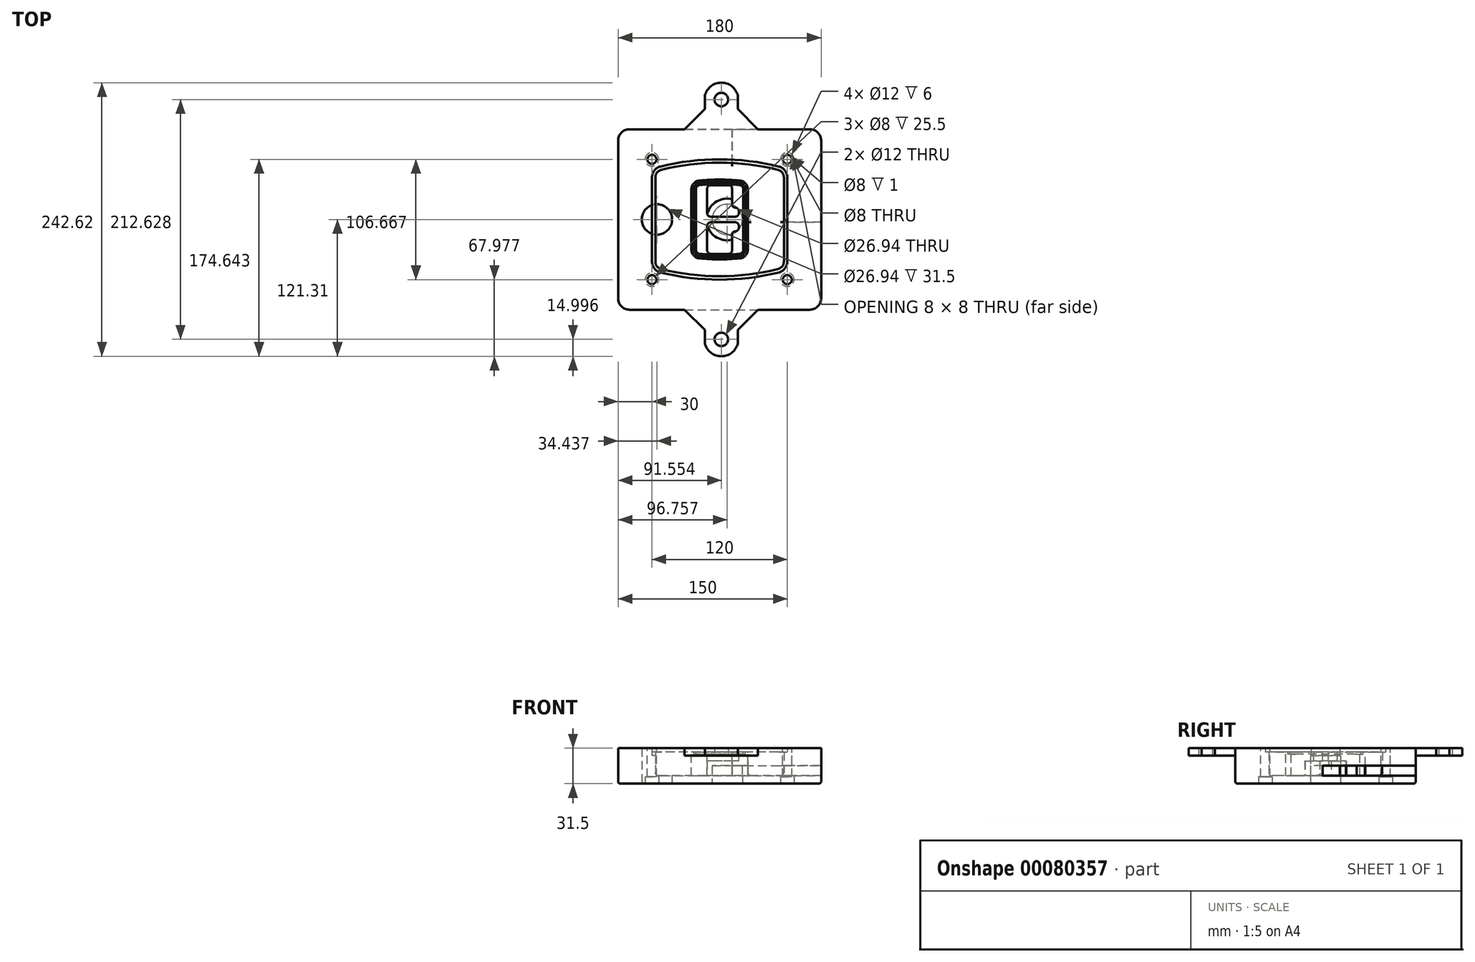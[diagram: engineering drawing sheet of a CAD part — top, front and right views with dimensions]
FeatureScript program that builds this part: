
annotation { "Feature Type Name" : "Feature", "Feature Type Description" : "" }
export const myFeature = defineFeature(function(context is Context, id is Id, definition is map)
    precondition{}
    {
        {
            var Q0;
            Q0=qCreatedBy(makeId("Top.planeOp"),FACE);
            var sketch = newSketch(context, id + "F0", { "sketchPlane" : qUnion([Q0])});
            skPoint(sketch, "E0.rect.middle", {"position": v(0, 0) * mm});
            skLineSegment(sketch, "E1.bottom", {"start": v(-80, -80) * mm, "end": v(80, -80) * mm});
            skLineSegment(sketch, "E1.top", {"start": v(-80, 80) * mm, "end": v(80, 80) * mm});
            skLineSegment(sketch, "E1.left", {"start": v(-90, -70) * mm, "end": v(-90, 70) * mm});
            skLineSegment(sketch, "E1.right", {"start": v(90, -70) * mm, "end": v(90, 70) * mm});
            skLineSegment(sketch, "E2", {"start": v(-90, 80) * mm, "end": v(90, -80) * mm, "construction": true});
            skLineSegment(sketch, "E3", {"start": v(90, 80) * mm, "end": v(-90, -80) * mm, "construction": true});
            skCircle(sketch, "E4", {"center": v(-60, 53.33) * mm, "radius": 4 * mm});
            skCircle(sketch, "E5", {"center": v(60, 53.33) * mm, "radius": 4 * mm});
            skCircle(sketch, "E6", {"center": v(60, -53.33) * mm, "radius": 4 * mm});
            skCircle(sketch, "E7", {"center": v(-60, -53.33) * mm, "radius": 4 * mm});
            skLineSegment(sketch, "E8", {"start": v(-60, 53.33) * mm, "end": v(60, 53.33) * mm, "construction": true});
            skLineSegment(sketch, "E9", {"start": v(60, 53.33) * mm, "end": v(60, -53.33) * mm, "construction": true});
            skLineSegment(sketch, "E10", {"start": v(60, -53.33) * mm, "end": v(-60, -53.33) * mm, "construction": true});
            skLineSegment(sketch, "E11", {"start": v(-60, -53.33) * mm, "end": v(-60, 53.33) * mm, "construction": true});
            skLineSegment(sketch, "E12", {"start": v(-60, 37.3) * mm, "end": v(-60, -37.3) * mm});
            skLineSegment(sketch, "E13", {"start": v(60, 37.3) * mm, "end": v(60, -37.3) * mm});
            skArc(sketch, "E14", {"start": v(52.38, 47.01) * mm, "mid": v(0, 53.33) * mm, "end": v(-52.38, 47.01) * mm});
            skArc(sketch, "E15", {"start": v(-52.38, -47.01) * mm, "mid": v(0, -53.33) * mm, "end": v(52.38, -47.01) * mm});
            skLineSegment(sketch, "E16", {"start": v(-60, 0) * mm, "end": v(60, 0) * mm, "construction": true});
            skPoint(sketch, "E17.visualSharp", {"position": v(-60, -45) * mm});
            skArc(sketch, "E17.filletArc", {"start": v(-60, -37.3) * mm, "mid": v(-57.87, -43.47) * mm, "end": v(-52.38, -47.01) * mm});
            skPoint(sketch, "E18.visualSharp", {"position": v(-60, 45) * mm});
            skArc(sketch, "E18.filletArc", {"start": v(-52.38, 47.01) * mm, "mid": v(-57.87, 43.47) * mm, "end": v(-60, 37.3) * mm});
            skPoint(sketch, "E19.visualSharp", {"position": v(60, 45) * mm});
            skArc(sketch, "E19.filletArc", {"start": v(60, 37.3) * mm, "mid": v(57.87, 43.47) * mm, "end": v(52.38, 47.01) * mm});
            skPoint(sketch, "E20.visualSharp", {"position": v(60, -45) * mm});
            skArc(sketch, "E20.filletArc", {"start": v(52.38, -47.01) * mm, "mid": v(57.87, -43.47) * mm, "end": v(60, -37.3) * mm});
            skPoint(sketch, "E21.visualSharp", {"position": v(-90, 80) * mm});
            skArc(sketch, "E21.filletArc", {"start": v(-80, 80) * mm, "mid": v(-87.07, 77.07) * mm, "end": v(-90, 70) * mm});
            skPoint(sketch, "E22.visualSharp", {"position": v(90, 80) * mm});
            skArc(sketch, "E22.filletArc", {"start": v(90, 70) * mm, "mid": v(87.07, 77.07) * mm, "end": v(80, 80) * mm});
            skPoint(sketch, "E23.visualSharp", {"position": v(90, -80) * mm});
            skArc(sketch, "E23.filletArc", {"start": v(80, -80) * mm, "mid": v(87.07, -77.07) * mm, "end": v(90, -70) * mm});
            skPoint(sketch, "E24.visualSharp", {"position": v(-90, -80) * mm});
            skArc(sketch, "E24.filletArc", {"start": v(-90, -70) * mm, "mid": v(-87.07, -77.07) * mm, "end": v(-80, -80) * mm});
            skArc(sketch, "E25.0", {"start": v(57, 37.3) * mm, "mid": v(55.5, 41.62) * mm, "end": v(51.67, 44.1) * mm});
            skLineSegment(sketch, "E25.1", {"start": v(57, 37.3) * mm, "end": v(57, -37.3) * mm});
            skArc(sketch, "E25.2", {"start": v(51.67, -44.1) * mm, "mid": v(55.5, -41.62) * mm, "end": v(57, -37.3) * mm});
            skArc(sketch, "E25.3", {"start": v(-51.67, -44.1) * mm, "mid": v(0, -50.33) * mm, "end": v(51.67, -44.1) * mm});
            skArc(sketch, "E25.4", {"start": v(-57, -37.3) * mm, "mid": v(-55.5, -41.62) * mm, "end": v(-51.67, -44.1) * mm});
            skArc(sketch, "E25.5", {"start": v(51.67, 44.1) * mm, "mid": v(0, 50.33) * mm, "end": v(-51.67, 44.1) * mm});
            skLineSegment(sketch, "E25.6", {"start": v(-57, 37.3) * mm, "end": v(-57, -37.3) * mm});
            skArc(sketch, "E25.7", {"start": v(-51.67, 44.1) * mm, "mid": v(-55.5, 41.62) * mm, "end": v(-57, 37.3) * mm});
            skArc(sketch, "E26.0", {"start": v(-53.33, 50.9) * mm, "mid": v(-61.01, 45.94) * mm, "end": v(-64, 37.3) * mm});
            skArc(sketch, "E26.1", {"start": v(53.33, 50.9) * mm, "mid": v(0, 57.33) * mm, "end": v(-53.33, 50.9) * mm});
            skArc(sketch, "E26.2", {"start": v(64, 37.3) * mm, "mid": v(61.01, 45.94) * mm, "end": v(53.33, 50.9) * mm});
            skLineSegment(sketch, "E26.3", {"start": v(64, 37.3) * mm, "end": v(64, -37.3) * mm});
            skArc(sketch, "E26.4", {"start": v(53.33, -50.9) * mm, "mid": v(61.01, -45.94) * mm, "end": v(64, -37.3) * mm});
            skLineSegment(sketch, "E26.5", {"start": v(-64, 37.3) * mm, "end": v(-64, -37.3) * mm});
            skArc(sketch, "E26.6", {"start": v(-53.33, -50.9) * mm, "mid": v(0, -57.33) * mm, "end": v(53.33, -50.9) * mm});
            skArc(sketch, "E26.7", {"start": v(-64, -37.3) * mm, "mid": v(-61.01, -45.94) * mm, "end": v(-53.33, -50.9) * mm});
            skSolve(sketch);
        }
        {
            var Q0;
            Q0=makeQuery(id+"F0.imprint","IMPRINT",FACE,{"disambiguationData":[TD([[makeQuery(id+"F0.imprint","IMPRINT",EDGE,{"derivedFrom":sQuery(id+"F0.wireOp",EDGE,"E1.bottom")}),1.0]])]});
            var Q1;
            Q1=makeQuery(id+"F0.imprint","IMPRINT",FACE,{"disambiguationData":[TD([[makeQuery(id+"F0.imprint","IMPRINT",EDGE,{"derivedFrom":sQuery(id+"F0.wireOp",EDGE,"E12")}),1.0]])]});
            var Q2;
            Q2=makeQuery(id+"F0.imprint","IMPRINT",FACE,{"disambiguationData":[TD([[makeQuery(id+"F0.imprint","IMPRINT",EDGE,{"derivedFrom":sQuery(id+"F0.wireOp",EDGE,"E25.0")}),1.0]])]});
            var Q3;
            Q3=makeQuery(id+"F0.imprint","IMPRINT",FACE,{"disambiguationData":[TD([[makeQuery(id+"F0.imprint","IMPRINT",EDGE,{"derivedFrom":sQuery(id+"F0.wireOp",EDGE,"E12")}),-1.0]])]});
            extrude(context, id + "F1", {"entities" : qUnion([Q0, Q1, Q2, Q3]), "oppositeDirection" : true, "depth" : 25 * mm});
        }
        {
            var Q0;
            Q0=makeQuery(id+"F0.imprint","IMPRINT",FACE,{"disambiguationData":[TD([[makeQuery(id+"F0.imprint","IMPRINT",EDGE,{"derivedFrom":sQuery(id+"F0.wireOp",EDGE,"E12")}),1.0]])]});
            extrude(context, id + "F2", {"entities" : qUnion([Q0]), "operationType" : NewBodyOperationType.ADD, "depth" : 3 * mm});
        }
        {
            var Q0;
            Q0=makeQuery(id+"F0.imprint","IMPRINT",FACE,{"disambiguationData":[TD([[makeQuery(id+"F0.imprint","IMPRINT",EDGE,{"derivedFrom":sQuery(id+"F0.wireOp",EDGE,"E25.0")}),1.0]])]});
            extrude(context, id + "F3", {"entities" : qUnion([Q0]), "operationType" : NewBodyOperationType.REMOVE, "oppositeDirection" : true, "depth" : 18 * mm});
        }
        {
            var Q0;
            Q0=makeQuery(id+"F2.opExtrude","CAP_FACE",FACE,{"disambiguationData":[OSD([sQuery(id+"F0.wireOp",EDGE,"E12"),sQuery(id+"F0.wireOp",EDGE,"E13"),sQuery(id+"F0.wireOp",EDGE,"E14"),sQuery(id+"F0.wireOp",EDGE,"E15"),sQuery(id+"F0.wireOp",EDGE,"E17.filletArc"),sQuery(id+"F0.wireOp",EDGE,"E18.filletArc"),sQuery(id+"F0.wireOp",EDGE,"E19.filletArc"),sQuery(id+"F0.wireOp",EDGE,"E20.filletArc"),sQuery(id+"F0.wireOp",EDGE,"E25.0"),sQuery(id+"F0.wireOp",EDGE,"E25.1"),sQuery(id+"F0.wireOp",EDGE,"E25.2"),sQuery(id+"F0.wireOp",EDGE,"E25.3"),sQuery(id+"F0.wireOp",EDGE,"E25.4"),sQuery(id+"F0.wireOp",EDGE,"E25.5"),sQuery(id+"F0.wireOp",EDGE,"E25.6"),sQuery(id+"F0.wireOp",EDGE,"E25.7")])],"isStart":false});
            var sketch = newSketch(context, id + "F4", { "sketchPlane" : qUnion([Q0])});
            skArc(sketch, "E27.0", {"start": v(-17.7, -34.56) * mm, "mid": v(0, -35.33) * mm, "end": v(17.7, -34.56) * mm});
            skArc(sketch, "E28.0", {"start": v(17.7, 34.56) * mm, "mid": v(0, 35.33) * mm, "end": v(-17.7, 34.56) * mm});
            skLineSegment(sketch, "E29", {"start": v(-25, 26.59) * mm, "end": v(-25, -26.59) * mm});
            skLineSegment(sketch, "E30", {"start": v(25, 26.59) * mm, "end": v(25, -26.59) * mm});
            skLineSegment(sketch, "E31", {"start": v(-25, 33.78) * mm, "end": v(25, 33.78) * mm, "construction": true});
            skLineSegment(sketch, "E32", {"start": v(-25, -33.78) * mm, "end": v(25, -33.78) * mm, "construction": true});
            skPoint(sketch, "E33.visualSharp", {"position": v(-25, 33.78) * mm});
            skArc(sketch, "E33.filletArc", {"start": v(-17.7, 34.56) * mm, "mid": v(-22.9, 32) * mm, "end": v(-25, 26.59) * mm});
            skPoint(sketch, "E34.visualSharp", {"position": v(25, 33.78) * mm});
            skArc(sketch, "E34.filletArc", {"start": v(25, 26.59) * mm, "mid": v(22.9, 32) * mm, "end": v(17.7, 34.56) * mm});
            skPoint(sketch, "E35.visualSharp", {"position": v(25, -33.78) * mm});
            skArc(sketch, "E35.filletArc", {"start": v(17.7, -34.56) * mm, "mid": v(22.9, -32) * mm, "end": v(25, -26.59) * mm});
            skPoint(sketch, "E36.visualSharp", {"position": v(-25, -33.78) * mm});
            skArc(sketch, "E36.filletArc", {"start": v(-25, -26.59) * mm, "mid": v(-22.9, -32) * mm, "end": v(-17.7, -34.56) * mm});
            skArc(sketch, "E37.0", {"start": v(51.67, 44.1) * mm, "mid": v(0, 50.33) * mm, "end": v(-51.67, 44.1) * mm});
            skArc(sketch, "E37.1", {"start": v(-51.67, 44.1) * mm, "mid": v(-55.5, 41.62) * mm, "end": v(-57, 37.3) * mm});
            skLineSegment(sketch, "E37.2", {"start": v(-57, 37.3) * mm, "end": v(-57, -37.3) * mm});
            skArc(sketch, "E37.3", {"start": v(-57, -37.3) * mm, "mid": v(-55.5, -41.62) * mm, "end": v(-51.67, -44.1) * mm});
            skArc(sketch, "E37.4", {"start": v(-51.67, -44.1) * mm, "mid": v(0, -50.33) * mm, "end": v(51.67, -44.1) * mm});
            skArc(sketch, "E37.5", {"start": v(51.67, -44.1) * mm, "mid": v(55.5, -41.62) * mm, "end": v(57, -37.3) * mm});
            skLineSegment(sketch, "E37.6", {"start": v(57, 37.3) * mm, "end": v(57, -37.3) * mm});
            skArc(sketch, "E37.7", {"start": v(57, 37.3) * mm, "mid": v(55.5, 41.62) * mm, "end": v(51.67, 44.1) * mm});
            skLineSegment(sketch, "E38.0", {"start": v(23, 26.59) * mm, "end": v(23, -26.59) * mm});
            skArc(sketch, "E38.1", {"start": v(17.53, -32.56) * mm, "mid": v(21.42, -30.64) * mm, "end": v(23, -26.59) * mm});
            skArc(sketch, "E38.2", {"start": v(-17.53, -32.56) * mm, "mid": v(0, -33.33) * mm, "end": v(17.53, -32.56) * mm});
            skArc(sketch, "E38.3", {"start": v(-23, -26.59) * mm, "mid": v(-21.42, -30.64) * mm, "end": v(-17.53, -32.56) * mm});
            skLineSegment(sketch, "E38.4", {"start": v(-23, 26.59) * mm, "end": v(-23, -26.59) * mm});
            skArc(sketch, "E38.5", {"start": v(23, 26.59) * mm, "mid": v(21.42, 30.64) * mm, "end": v(17.53, 32.56) * mm});
            skArc(sketch, "E38.6", {"start": v(-17.53, 32.56) * mm, "mid": v(-21.42, 30.64) * mm, "end": v(-23, 26.59) * mm});
            skArc(sketch, "E38.7", {"start": v(17.53, 32.56) * mm, "mid": v(0, 33.33) * mm, "end": v(-17.53, 32.56) * mm});
            skArc(sketch, "E39.0", {"start": v(21, 26.59) * mm, "mid": v(19.95, 29.29) * mm, "end": v(17.35, 30.57) * mm});
            skLineSegment(sketch, "E39.1", {"start": v(21, 26.59) * mm, "end": v(21, -26.59) * mm});
            skArc(sketch, "E39.2", {"start": v(17.35, -30.57) * mm, "mid": v(19.95, -29.29) * mm, "end": v(21, -26.59) * mm});
            skArc(sketch, "E39.3", {"start": v(-17.35, -30.57) * mm, "mid": v(0, -31.33) * mm, "end": v(17.35, -30.57) * mm});
            skArc(sketch, "E39.4", {"start": v(-21, -26.59) * mm, "mid": v(-19.95, -29.29) * mm, "end": v(-17.35, -30.57) * mm});
            skArc(sketch, "E39.5", {"start": v(17.35, 30.57) * mm, "mid": v(0, 31.33) * mm, "end": v(-17.35, 30.57) * mm});
            skLineSegment(sketch, "E39.6", {"start": v(-21, 26.59) * mm, "end": v(-21, -26.59) * mm});
            skArc(sketch, "E39.7", {"start": v(-17.35, 30.57) * mm, "mid": v(-19.95, 29.29) * mm, "end": v(-21, 26.59) * mm});
            skLineSegment(sketch, "E40", {"start": v(-25, 0) * mm, "end": v(25, 0) * mm, "construction": true});
            skLineSegment(sketch, "E41", {"start": v(-11, 5.5) * mm, "end": v(-11, 27.5) * mm});
            skLineSegment(sketch, "E42", {"start": v(-8, 30.5) * mm, "end": v(8, 30.5) * mm});
            skLineSegment(sketch, "E43", {"start": v(11, 27.5) * mm, "end": v(11, 13.5) * mm});
            skLineSegment(sketch, "E44", {"start": v(14, 10.5) * mm, "end": v(14, 10.5) * mm});
            skLineSegment(sketch, "E45", {"start": v(17, 7.5) * mm, "end": v(17, 5.5) * mm});
            skLineSegment(sketch, "E46", {"start": v(14, 2.5) * mm, "end": v(-8, 2.5) * mm});
            skPoint(sketch, "E47.visualSharp", {"position": v(-11, 30.5) * mm});
            skArc(sketch, "E47.filletArc", {"start": v(-8, 30.5) * mm, "mid": v(-10.12, 29.62) * mm, "end": v(-11, 27.5) * mm});
            skPoint(sketch, "E48.visualSharp", {"position": v(11, 30.5) * mm});
            skArc(sketch, "E48.filletArc", {"start": v(11, 27.5) * mm, "mid": v(10.12, 29.62) * mm, "end": v(8, 30.5) * mm});
            skPoint(sketch, "E49.visualSharp", {"position": v(11, 10.5) * mm});
            skArc(sketch, "E49.filletArc", {"start": v(11, 13.5) * mm, "mid": v(11.88, 11.38) * mm, "end": v(14, 10.5) * mm});
            skPoint(sketch, "E50.visualSharp", {"position": v(17, 10.5) * mm});
            skArc(sketch, "E50.filletArc", {"start": v(17, 7.5) * mm, "mid": v(16.12, 9.62) * mm, "end": v(14, 10.5) * mm});
            skPoint(sketch, "E51.visualSharp", {"position": v(17, 2.5) * mm});
            skArc(sketch, "E51.filletArc", {"start": v(14, 2.5) * mm, "mid": v(16.12, 3.38) * mm, "end": v(17, 5.5) * mm});
            skPoint(sketch, "E52.visualSharp", {"position": v(-11, 2.5) * mm});
            skArc(sketch, "E52.filletArc", {"start": v(-11, 5.5) * mm, "mid": v(-10.12, 3.38) * mm, "end": v(-8, 2.5) * mm});
            skLineSegment(sketch, "E53.0.MirrorCS", {"start": v(14, -2.5) * mm, "end": v(-8, -2.5) * mm});
            skArc(sketch, "E54.0.MirrorCS", {"start": v(-11, -5.5) * mm, "mid": v(-10.12, -3.38) * mm, "end": v(-8, -2.5) * mm});
            skLineSegment(sketch, "E55.0.MirrorCS", {"start": v(-11, -5.5) * mm, "end": v(-11, -27.5) * mm});
            skArc(sketch, "E56.0.MirrorCS", {"start": v(-8, -30.5) * mm, "mid": v(-10.12, -29.62) * mm, "end": v(-11, -27.5) * mm});
            skLineSegment(sketch, "E57.0.MirrorCS", {"start": v(-8, -30.5) * mm, "end": v(8, -30.5) * mm});
            skArc(sketch, "E58.0.MirrorCS", {"start": v(11, -27.5) * mm, "mid": v(10.12, -29.62) * mm, "end": v(8, -30.5) * mm});
            skLineSegment(sketch, "E59.0.MirrorCS", {"start": v(11, -27.5) * mm, "end": v(11, -13.5) * mm});
            skArc(sketch, "E60.0.MirrorCS", {"start": v(11, -13.5) * mm, "mid": v(11.88, -11.38) * mm, "end": v(14, -10.5) * mm});
            skArc(sketch, "E61.0.MirrorCS", {"start": v(17, -7.5) * mm, "mid": v(16.12, -9.62) * mm, "end": v(14, -10.5) * mm});
            skLineSegment(sketch, "E62.0.MirrorCS", {"start": v(17, -7.5) * mm, "end": v(17, -5.5) * mm});
            skArc(sketch, "E63.0.MirrorCS", {"start": v(14, -2.5) * mm, "mid": v(16.12, -3.38) * mm, "end": v(17, -5.5) * mm});
            skSolve(sketch);
        }
        {
            var Q0;
            Q0=makeQuery(id+"F4.imprint","IMPRINT",FACE,{"disambiguationData":[TD([[makeQuery(id+"F4.imprint","IMPRINT",EDGE,{"derivedFrom":sQuery(id+"F4.wireOp",EDGE,"E27.0")}),1.0]])]});
            var Q1;
            Q1=makeQuery(id+"F4.imprint","IMPRINT",FACE,{"disambiguationData":[TD([[makeQuery(id+"F4.imprint","IMPRINT",EDGE,{"derivedFrom":sQuery(id+"F4.wireOp",EDGE,"E38.0")}),-1.0]])]});
            var Q2;
            Q2=makeQuery(id+"F4.imprint","IMPRINT",FACE,{"disambiguationData":[TD([[makeQuery(id+"F4.imprint","IMPRINT",EDGE,{"derivedFrom":sQuery(id+"F4.wireOp",EDGE,"E39.0")}),1.0]])]});
            extrude(context, id + "F5", {"entities" : qUnion([Q0, Q1, Q2]), "operationType" : NewBodyOperationType.ADD, "endBound" : BoundingType.UP_TO_NEXT, "oppositeDirection" : true, "depth" : 25 * mm});
        }
        {
            var Q0;
            Q0=makeQuery(id+"F4.imprint","IMPRINT",FACE,{"disambiguationData":[TD([[makeQuery(id+"F4.imprint","IMPRINT",EDGE,{"derivedFrom":sQuery(id+"F4.wireOp",EDGE,"E38.0")}),-1.0]])]});
            extrude(context, id + "F6", {"entities" : qUnion([Q0]), "operationType" : NewBodyOperationType.REMOVE, "oppositeDirection" : true, "depth" : 2 * mm});
        }
        {
            var Q0;
            Q0=makeQuery(id+"F1.opExtrude","CAP_FACE",FACE,{"disambiguationData":[OSD([sQuery(id+"F0.wireOp",EDGE,"E1.bottom"),sQuery(id+"F0.wireOp",EDGE,"E1.top"),sQuery(id+"F0.wireOp",EDGE,"E1.left"),sQuery(id+"F0.wireOp",EDGE,"E1.right"),sQuery(id+"F0.wireOp",EDGE,"E4"),sQuery(id+"F0.wireOp",EDGE,"E5"),sQuery(id+"F0.wireOp",EDGE,"E6"),sQuery(id+"F0.wireOp",EDGE,"E7"),sQuery(id+"F0.wireOp",EDGE,"E21.filletArc"),sQuery(id+"F0.wireOp",EDGE,"E22.filletArc"),sQuery(id+"F0.wireOp",EDGE,"E23.filletArc"),sQuery(id+"F0.wireOp",EDGE,"E24.filletArc")])],"isStart":false});
            var sketch = newSketch(context, id + "F7", { "sketchPlane" : qUnion([Q0])});
            skCircle(sketch, "E64", {"center": v(6.76, 0) * mm, "radius": 13.47 * mm});
            skCircle(sketch, "E65", {"center": v(-55.56, 0) * mm, "radius": 13.47 * mm});
            skLineSegment(sketch, "E66", {"start": v(90, 0) * mm, "end": v(-90, 0) * mm});
            skCircle(sketch, "E67", {"center": v(6.76, 0) * mm, "radius": 18.47 * mm});
            skCircle(sketch, "E68", {"center": v(60, -53.33) * mm, "radius": 6 * mm});
            skCircle(sketch, "E69", {"center": v(-60, -53.33) * mm, "radius": 6 * mm});
            skCircle(sketch, "E70", {"center": v(-60, 53.33) * mm, "radius": 6 * mm});
            skCircle(sketch, "E71", {"center": v(60, 53.33) * mm, "radius": 6 * mm});
            skSolve(sketch);
        }
        {
            var Q0;
            {var subQ1=sQuery(id+"F7.wireOp",EDGE,"E66");var subQ4=sQuery(id+"F7.wireOp",EDGE,"E64");var subQ6=makeQuery(id+"F7.imprint","INTERSECT",VERTEX,{"disambiguationData":[OD(0.0)],"derivedFrom":[subQ4,subQ1]});Q0=makeQuery(id+"F7.imprint","IMPRINT",FACE,{"disambiguationData":[TD([[makeQuery(id+"F7.imprint","IMPRINT",EDGE,{"disambiguationData":[TD([[subQ6,-1.0]])],"derivedFrom":subQ4}),-1.0]])]});}
            var Q1;
            {var subQ0=sQuery(id+"F7.wireOp",EDGE,"E66");var subQ1=sQuery(id+"F7.wireOp",EDGE,"E64");var subQ3=makeQuery(id+"F7.imprint","INTERSECT",VERTEX,{"disambiguationData":[OD(0.0)],"derivedFrom":[subQ1,subQ0]});Q1=makeQuery(id+"F7.imprint","IMPRINT",FACE,{"disambiguationData":[TD([[makeQuery(id+"F7.imprint","IMPRINT",EDGE,{"disambiguationData":[TD([[subQ3,-1.0]])],"derivedFrom":subQ1}),1.0]])]});}
            var Q2;
            {var subQ0=sQuery(id+"F7.wireOp",EDGE,"E66");var subQ1=sQuery(id+"F7.wireOp",EDGE,"E64");var subQ3=makeQuery(id+"F7.imprint","INTERSECT",VERTEX,{"disambiguationData":[OD(0.0)],"derivedFrom":[subQ1,subQ0]});Q2=makeQuery(id+"F7.imprint","IMPRINT",FACE,{"disambiguationData":[TD([[makeQuery(id+"F7.imprint","IMPRINT",EDGE,{"disambiguationData":[TD([[subQ3,1.0]])],"derivedFrom":subQ1}),1.0]])]});}
            var Q3;
            {var subQ1=sQuery(id+"F7.wireOp",EDGE,"E66");var subQ4=sQuery(id+"F7.wireOp",EDGE,"E64");var subQ6=makeQuery(id+"F7.imprint","INTERSECT",VERTEX,{"disambiguationData":[OD(0.0)],"derivedFrom":[subQ4,subQ1]});Q3=makeQuery(id+"F7.imprint","IMPRINT",FACE,{"disambiguationData":[TD([[makeQuery(id+"F7.imprint","IMPRINT",EDGE,{"disambiguationData":[TD([[subQ6,1.0]])],"derivedFrom":subQ4}),-1.0]])]});}
            extrude(context, id + "F8", {"entities" : qUnion([Q0, Q1, Q2, Q3]), "operationType" : NewBodyOperationType.ADD, "oppositeDirection" : true, "depth" : 20 * mm});
        }
        {
            var Q0;
            {var subQ0=sQuery(id+"F7.wireOp",EDGE,"E66");var subQ1=sQuery(id+"F7.wireOp",EDGE,"E64");var subQ3=makeQuery(id+"F7.imprint","INTERSECT",VERTEX,{"disambiguationData":[OD(0.0)],"derivedFrom":[subQ1,subQ0]});Q0=makeQuery(id+"F7.imprint","IMPRINT",FACE,{"disambiguationData":[TD([[makeQuery(id+"F7.imprint","IMPRINT",EDGE,{"disambiguationData":[TD([[subQ3,-1.0]])],"derivedFrom":subQ1}),1.0]])]});}
            var Q1;
            {var subQ0=sQuery(id+"F7.wireOp",EDGE,"E66");var subQ1=sQuery(id+"F7.wireOp",EDGE,"E64");var subQ3=makeQuery(id+"F7.imprint","INTERSECT",VERTEX,{"disambiguationData":[OD(0.0)],"derivedFrom":[subQ1,subQ0]});Q1=makeQuery(id+"F7.imprint","IMPRINT",FACE,{"disambiguationData":[TD([[makeQuery(id+"F7.imprint","IMPRINT",EDGE,{"disambiguationData":[TD([[subQ3,1.0]])],"derivedFrom":subQ1}),1.0]])]});}
            extrude(context, id + "F9", {"entities" : qUnion([Q0, Q1]), "operationType" : NewBodyOperationType.REMOVE, "oppositeDirection" : true, "depth" : 16 * mm});
        }
        {
            var Q0;
            {var subQ0=sQuery(id+"F7.wireOp",EDGE,"E66");var subQ1=sQuery(id+"F7.wireOp",EDGE,"E65");var subQ3=makeQuery(id+"F7.imprint","INTERSECT",VERTEX,{"disambiguationData":[OD(0.0)],"derivedFrom":[subQ1,subQ0]});Q0=makeQuery(id+"F7.imprint","IMPRINT",FACE,{"disambiguationData":[TD([[makeQuery(id+"F7.imprint","IMPRINT",EDGE,{"disambiguationData":[TD([[subQ3,-1.0]])],"derivedFrom":subQ1}),1.0]])]});}
            var Q1;
            {var subQ0=sQuery(id+"F7.wireOp",EDGE,"E66");var subQ1=sQuery(id+"F7.wireOp",EDGE,"E65");var subQ3=makeQuery(id+"F7.imprint","INTERSECT",VERTEX,{"disambiguationData":[OD(0.0)],"derivedFrom":[subQ1,subQ0]});Q1=makeQuery(id+"F7.imprint","IMPRINT",FACE,{"disambiguationData":[TD([[makeQuery(id+"F7.imprint","IMPRINT",EDGE,{"disambiguationData":[TD([[subQ3,1.0]])],"derivedFrom":subQ1}),1.0]])]});}
            extrude(context, id + "F10", {"entities" : qUnion([Q0, Q1]), "operationType" : NewBodyOperationType.REMOVE, "oppositeDirection" : true, "depth" : 25 * mm});
        }
        {
            var Q0;
            Q0=makeQuery(id+"F7.imprint","IMPRINT",FACE,{"disambiguationData":[TD([[makeQuery(id+"F7.imprint","IMPRINT",EDGE,{"derivedFrom":sQuery(id+"F7.wireOp",EDGE,"E68")}),1.0]])]});
            var Q1;
            Q1=makeQuery(id+"F7.imprint","IMPRINT",FACE,{"disambiguationData":[TD([[makeQuery(id+"F7.imprint","IMPRINT",EDGE,{"derivedFrom":makeQuery(id+"F1.opExtrude","CAP_EDGE",EDGE,{"disambiguationData":[OSD([sQuery(id+"F0.wireOp",EDGE,"E5")])],"isStart":false})}),-1.0]])]});
            var Q2;
            Q2=makeQuery(id+"F7.imprint","IMPRINT",FACE,{"disambiguationData":[TD([[makeQuery(id+"F7.imprint","IMPRINT",EDGE,{"derivedFrom":sQuery(id+"F7.wireOp",EDGE,"E69")}),1.0]])]});
            var Q3;
            Q3=makeQuery(id+"F7.imprint","IMPRINT",FACE,{"disambiguationData":[TD([[makeQuery(id+"F7.imprint","IMPRINT",EDGE,{"derivedFrom":makeQuery(id+"F1.opExtrude","CAP_EDGE",EDGE,{"disambiguationData":[OSD([sQuery(id+"F0.wireOp",EDGE,"E4")])],"isStart":false})}),-1.0]])]});
            var Q4;
            Q4=makeQuery(id+"F7.imprint","IMPRINT",FACE,{"disambiguationData":[TD([[makeQuery(id+"F7.imprint","IMPRINT",EDGE,{"derivedFrom":sQuery(id+"F7.wireOp",EDGE,"E70")}),1.0]])]});
            var Q5;
            Q5=makeQuery(id+"F7.imprint","IMPRINT",FACE,{"disambiguationData":[TD([[makeQuery(id+"F7.imprint","IMPRINT",EDGE,{"derivedFrom":makeQuery(id+"F1.opExtrude","CAP_EDGE",EDGE,{"disambiguationData":[OSD([sQuery(id+"F0.wireOp",EDGE,"E7")])],"isStart":false})}),-1.0]])]});
            var Q6;
            Q6=makeQuery(id+"F7.imprint","IMPRINT",FACE,{"disambiguationData":[TD([[makeQuery(id+"F7.imprint","IMPRINT",EDGE,{"derivedFrom":sQuery(id+"F7.wireOp",EDGE,"E71")}),1.0]])]});
            var Q7;
            Q7=makeQuery(id+"F7.imprint","IMPRINT",FACE,{"disambiguationData":[TD([[makeQuery(id+"F7.imprint","IMPRINT",EDGE,{"derivedFrom":makeQuery(id+"F1.opExtrude","CAP_EDGE",EDGE,{"disambiguationData":[OSD([sQuery(id+"F0.wireOp",EDGE,"E6")])],"isStart":false})}),-1.0]])]});
            extrude(context, id + "F11", {"entities" : qUnion([Q0, Q1, Q2, Q3, Q4, Q5, Q6, Q7]), "operationType" : NewBodyOperationType.REMOVE, "oppositeDirection" : true, "depth" : 6 * mm});
        }
        {
            var Q0;
            Q0=makeQuery(id+"F9.boolean.opBoolean","COPY",FACE,{"derivedFrom":makeQuery(id+"F9.opExtrude","CAP_FACE",FACE,{"disambiguationData":[OSD([sQuery(id+"F7.wireOp",EDGE,"E64")])],"isStart":false})});
            var sketch = newSketch(context, id + "F12", { "sketchPlane" : qUnion([Q0])});
            skArc(sketch, "E72.0", {"start": v(11, -88.19) * mm, "mid": v(97.1, -83.6) * mm, "end": v(92.5, 2.5) * mm});
            skLineSegment(sketch, "E72.1", {"start": v(11, -17.97) * mm, "end": v(11, -17.97) * mm});
            skLineSegment(sketch, "E73", {"start": v(92.5, -105.13) * mm, "end": v(102.3, -105.13) * mm});
            skLineSegment(sketch, "E74.0", {"start": v(92.5, 2.5) * mm, "end": v(14, 2.5) * mm});
            skArc(sketch, "E74.1", {"start": v(14, 2.5) * mm, "mid": v(16.12, 3.38) * mm, "end": v(17, 5.5) * mm});
            skLineSegment(sketch, "E74.2", {"start": v(17, 7.5) * mm, "end": v(17, 5.5) * mm});
            skArc(sketch, "E74.3", {"start": v(17, 7.5) * mm, "mid": v(16.12, 9.62) * mm, "end": v(14, 10.5) * mm});
            skArc(sketch, "E74.4", {"start": v(11, 13.5) * mm, "mid": v(11.88, 11.38) * mm, "end": v(14, 10.5) * mm});
            skLineSegment(sketch, "E74.5", {"start": v(11, 13.5) * mm, "end": v(11, -88.19) * mm});
            skLineSegment(sketch, "E74.7", {"start": v(92.5, -2.5) * mm, "end": v(14, -2.5) * mm});
            skArc(sketch, "E74.8", {"start": v(14, -2.5) * mm, "mid": v(16.12, -3.38) * mm, "end": v(17, -5.5) * mm});
            skLineSegment(sketch, "E74.9", {"start": v(17, -7.5) * mm, "end": v(17, -5.5) * mm});
            skArc(sketch, "E74.10", {"start": v(17, -7.5) * mm, "mid": v(16.12, -9.62) * mm, "end": v(14, -10.5) * mm});
            skArc(sketch, "E74.11", {"start": v(11, -13.5) * mm, "mid": v(11.88, -11.38) * mm, "end": v(14, -10.5) * mm});
            skLineSegment(sketch, "E74.12", {"start": v(11, -17.97) * mm, "end": v(11, -13.5) * mm});
            skPoint(sketch, "E75.orphan", {"position": v(11, -27.5) * mm});
            skPoint(sketch, "E76.orphan", {"position": v(-8, -2.5) * mm});
            skPoint(sketch, "E77.orphan", {"position": v(-8, 2.5) * mm});
            skPoint(sketch, "E78.orphan", {"position": v(11, 27.5) * mm});
            skSolve(sketch);
        }
        {
            var Q0;
            {var subQ7=sQuery(id+"F12.wireOp",EDGE,"E72.0");var subQ14=sQuery(id+"F12.wireOp",EDGE,"E72.1");var subQ16=sQuery(id+"F12.wireOp",EDGE,"E74.1");var subQ18=sQuery(id+"F12.wireOp",EDGE,"E74.8");Q0=qUnion([makeQuery(id+"F12.imprint","IMPRINT",FACE,{"disambiguationData":[TD([[makeQuery(id+"F12.imprint","IMPRINT",EDGE,{"derivedFrom":subQ7}),1.0]])]}),makeQuery(id+"F12.imprint","IMPRINT",FACE,{"disambiguationData":[TD([[makeQuery(id+"F12.imprint","IMPRINT",EDGE,{"derivedFrom":subQ14}),1.0]])]}),makeQuery(id+"F12.imprint","IMPRINT",FACE,{"disambiguationData":[TD([[makeQuery(id+"F12.imprint","IMPRINT",EDGE,{"derivedFrom":subQ16}),1.0]])]}),makeQuery(id+"F12.imprint","IMPRINT",FACE,{"disambiguationData":[TD([[makeQuery(id+"F12.imprint","IMPRINT",EDGE,{"derivedFrom":subQ18}),-1.0]])]})]);}
            var Q1;
            Q1=makeQuery(id+"F5.boolean.opBoolean","SPLIT",FACE,{"disambiguationData":[TD([makeQuery(id+"F5.opExtrude","SWEPT_FACE",FACE,{"disambiguationData":[OSD([sQuery(id+"F4.wireOp",EDGE,"E41")])]})])],"derivedFrom":makeQuery(id+"F3.boolean.opBoolean","COPY",FACE,{"derivedFrom":makeQuery(id+"F3.opExtrude","CAP_FACE",FACE,{"disambiguationData":[OSD([sQuery(id+"F0.wireOp",EDGE,"E25.0"),sQuery(id+"F0.wireOp",EDGE,"E25.1"),sQuery(id+"F0.wireOp",EDGE,"E25.2"),sQuery(id+"F0.wireOp",EDGE,"E25.3"),sQuery(id+"F0.wireOp",EDGE,"E25.4"),sQuery(id+"F0.wireOp",EDGE,"E25.5"),sQuery(id+"F0.wireOp",EDGE,"E25.6"),sQuery(id+"F0.wireOp",EDGE,"E25.7")])],"isStart":false})})});
            extrude(context, id + "F13", {"entities" : qUnion([Q0]), "operationType" : NewBodyOperationType.REMOVE, "endBound" : BoundingType.UP_TO_SURFACE, "endBoundEntityFace" : qUnion([Q1]), "depth" : 25 * mm});
        }
        {
            var Q0;
            Q0=makeQuery(id+"F3.boolean.opBoolean","COPY",EDGE,{"derivedFrom":makeQuery(id+"F3.opExtrude","CAP_EDGE",EDGE,{"disambiguationData":[OSD([sQuery(id+"F0.wireOp",EDGE,"E25.6")])],"isStart":false})});
            var Q1;
            Q1=makeQuery(id+"F8.boolean.opBoolean","INTERSECT",EDGE,{"derivedFrom":[makeQuery(id+"F5.opExtrude","SWEPT_FACE",FACE,{"disambiguationData":[OSD([sQuery(id+"F4.wireOp",EDGE,"E30")])]}),makeQuery(id+"F8.opExtrude","CAP_FACE",FACE,{"disambiguationData":[OSD([sQuery(id+"F7.wireOp",EDGE,"E67")])],"isStart":false})]});
            var Q2;
            Q2=makeQuery(id+"F8.boolean.opBoolean","INTERSECT",EDGE,{"disambiguationData":[OD(1.0)],"derivedFrom":[makeQuery(id+"F5.opExtrude","SWEPT_FACE",FACE,{"disambiguationData":[OSD([sQuery(id+"F4.wireOp",EDGE,"E30")])]}),makeQuery(id+"F8.opExtrude","SWEPT_FACE",FACE,{"disambiguationData":[OSD([sQuery(id+"F7.wireOp",EDGE,"E67")])]})]});
            var Q3;
            {var subQ0=makeQuery(id+"F3.boolean.opBoolean","COPY",FACE,{"derivedFrom":makeQuery(id+"F3.opExtrude","CAP_FACE",FACE,{"disambiguationData":[OSD([sQuery(id+"F0.wireOp",EDGE,"E25.0"),sQuery(id+"F0.wireOp",EDGE,"E25.1"),sQuery(id+"F0.wireOp",EDGE,"E25.2"),sQuery(id+"F0.wireOp",EDGE,"E25.3"),sQuery(id+"F0.wireOp",EDGE,"E25.4"),sQuery(id+"F0.wireOp",EDGE,"E25.5"),sQuery(id+"F0.wireOp",EDGE,"E25.6"),sQuery(id+"F0.wireOp",EDGE,"E25.7")])],"isStart":false})});var subQ1=sQuery(id+"F4.wireOp",EDGE,"E30");Q3=makeQuery(id+"F8.boolean.opBoolean","SPLIT",EDGE,{"disambiguationData":[TD([makeQuery(id+"F5.opExtrude","SWEPT_FACE",FACE,{"disambiguationData":[OSD([sQuery(id+"F4.wireOp",EDGE,"E35.filletArc")])]})])],"derivedFrom":makeQuery(id+"F5.opExtrude","TWEAK_EDGE",EDGE,{"derivedFrom":[subQ0,makeQuery(id+"F4.imprint","IMPRINT",EDGE,{"derivedFrom":subQ1})]})});}
            var Q4;
            {var subQ0=sQuery(id+"F0.wireOp",EDGE,"E25.0");var subQ1=sQuery(id+"F0.wireOp",EDGE,"E25.1");var subQ2=sQuery(id+"F0.wireOp",EDGE,"E25.2");var subQ3=sQuery(id+"F0.wireOp",EDGE,"E25.3");var subQ4=sQuery(id+"F0.wireOp",EDGE,"E25.4");var subQ5=sQuery(id+"F0.wireOp",EDGE,"E25.5");var subQ6=sQuery(id+"F0.wireOp",EDGE,"E25.6");var subQ7=sQuery(id+"F0.wireOp",EDGE,"E25.7");Q4=makeQuery(id+"F8.boolean.opBoolean","INTERSECT",EDGE,{"derivedFrom":[makeQuery(id+"F5.boolean.opBoolean","SPLIT",FACE,{"disambiguationData":[TD([makeQuery(id+"F2.opExtrude","SWEPT_FACE",FACE,{"disambiguationData":[OSD([subQ0])]})])],"derivedFrom":makeQuery(id+"F3.boolean.opBoolean","COPY",FACE,{"derivedFrom":makeQuery(id+"F3.opExtrude","CAP_FACE",FACE,{"disambiguationData":[OSD([subQ0,subQ1,subQ2,subQ3,subQ4,subQ5,subQ6,subQ7])],"isStart":false})})}),makeQuery(id+"F8.opExtrude","SWEPT_FACE",FACE,{"disambiguationData":[OSD([sQuery(id+"F7.wireOp",EDGE,"E67")])]})]});}
            var Q5;
            Q5=makeQuery(id+"F8.boolean.opBoolean","INTERSECT",EDGE,{"disambiguationData":[OD(0.0)],"derivedFrom":[makeQuery(id+"F5.opExtrude","SWEPT_FACE",FACE,{"disambiguationData":[OSD([sQuery(id+"F4.wireOp",EDGE,"E30")])]}),makeQuery(id+"F8.opExtrude","SWEPT_FACE",FACE,{"disambiguationData":[OSD([sQuery(id+"F7.wireOp",EDGE,"E67")])]})]});
            fillet(context, id + "F14", {"entities" : qUnion([Q0, Q1, Q2, Q3, Q4, Q5]), "radius" : 3 * mm, "tangentPropagation" : true, "allowEdgeOverflow" : false});
        }
        {
            var Q0;
            Q0=makeQuery(id+"F1.opExtrude","CAP_EDGE",EDGE,{"disambiguationData":[OSD([sQuery(id+"F0.wireOp",EDGE,"E1.bottom")])],"isStart":false});
            fillet(context, id + "F15", {"entities" : qUnion([Q0]), "radius" : 2 * mm, "tangentPropagation" : true, "allowEdgeOverflow" : false});
        }
        {
            var Q0;
            {var subQ0=sQuery(id+"F0.wireOp",EDGE,"E22.filletArc");var subQ1=sQuery(id+"F0.wireOp",EDGE,"E7");var subQ2=sQuery(id+"F0.wireOp",EDGE,"E6");var subQ3=sQuery(id+"F0.wireOp",EDGE,"E5");var subQ4=sQuery(id+"F0.wireOp",EDGE,"E4");var subQ5=sQuery(id+"F0.wireOp",EDGE,"E1.bottom");var subQ6=sQuery(id+"F0.wireOp",EDGE,"E21.filletArc");var subQ7=sQuery(id+"F0.wireOp",EDGE,"E1.top");var subQ8=sQuery(id+"F0.wireOp",EDGE,"E1.left");var subQ9=sQuery(id+"F0.wireOp",EDGE,"E1.right");var subQ10=sQuery(id+"F0.wireOp",EDGE,"E23.filletArc");var subQ11=sQuery(id+"F0.wireOp",EDGE,"E24.filletArc");Q0=makeQuery(id+"F2.boolean.opBoolean","SPLIT",FACE,{"disambiguationData":[TD([makeQuery(id+"F1.opExtrude","SWEPT_FACE",FACE,{"disambiguationData":[OSD([subQ5])]})])],"derivedFrom":makeQuery(id+"F1.opExtrude","CAP_FACE",FACE,{"disambiguationData":[OSD([subQ5,subQ7,subQ8,subQ9,subQ4,subQ3,subQ2,subQ1,subQ6,subQ0,subQ10,subQ11])],"isStart":true})});}
            var sketch = newSketch(context, id + "F16", { "sketchPlane" : qUnion([Q0])});
            skLineSegment(sketch, "E79.0", {"start": v(-80, 80) * mm, "end": v(80, 80) * mm});
            skArc(sketch, "E79.1", {"start": v(-80, 80) * mm, "mid": v(-87.07, 77.07) * mm, "end": v(-90, 70) * mm});
            skLineSegment(sketch, "E79.2", {"start": v(-90, -70) * mm, "end": v(-90, 70) * mm});
            skArc(sketch, "E79.3", {"start": v(-90, -70) * mm, "mid": v(-87.07, -77.07) * mm, "end": v(-80, -80) * mm});
            skLineSegment(sketch, "E79.4", {"start": v(-80, -80) * mm, "end": v(80, -80) * mm});
            skArc(sketch, "E79.5", {"start": v(80, -80) * mm, "mid": v(87.07, -77.07) * mm, "end": v(90, -70) * mm});
            skLineSegment(sketch, "E79.6", {"start": v(90, -70) * mm, "end": v(90, 70) * mm});
            skArc(sketch, "E79.7", {"start": v(90, 70) * mm, "mid": v(87.07, 77.07) * mm, "end": v(80, 80) * mm});
            skCircle(sketch, "E79.8", {"center": v(60, 53.33) * mm, "radius": 4 * mm});
            skCircle(sketch, "E79.9", {"center": v(-60, 53.33) * mm, "radius": 4 * mm});
            skCircle(sketch, "E79.10", {"center": v(-60, -53.33) * mm, "radius": 4 * mm});
            skCircle(sketch, "E79.11", {"center": v(60, -53.33) * mm, "radius": 4 * mm});
            skLineSegment(sketch, "E79.12", {"start": v(60, 37.3) * mm, "end": v(60, -37.3) * mm});
            skArc(sketch, "E79.13", {"start": v(60, 37.3) * mm, "mid": v(57.87, 43.47) * mm, "end": v(52.38, 47.01) * mm});
            skArc(sketch, "E79.14", {"start": v(52.38, 47.01) * mm, "mid": v(0, 53.33) * mm, "end": v(-52.38, 47.01) * mm});
            skArc(sketch, "E79.15", {"start": v(-52.38, 47.01) * mm, "mid": v(-57.87, 43.47) * mm, "end": v(-60, 37.3) * mm});
            skLineSegment(sketch, "E79.16", {"start": v(-60, 37.3) * mm, "end": v(-60, -37.3) * mm});
            skArc(sketch, "E79.17", {"start": v(-60, -37.3) * mm, "mid": v(-57.87, -43.47) * mm, "end": v(-52.38, -47.01) * mm});
            skArc(sketch, "E79.18", {"start": v(-52.38, -47.01) * mm, "mid": v(0, -53.33) * mm, "end": v(52.38, -47.01) * mm});
            skArc(sketch, "E79.19", {"start": v(52.38, -47.01) * mm, "mid": v(57.87, -43.47) * mm, "end": v(60, -37.3) * mm});
            skLineSegment(sketch, "E80", {"start": v(-30.99, 80) * mm, "end": v(-12.99, 98) * mm});
            skLineSegment(sketch, "E81", {"start": v(34.1, 80) * mm, "end": v(16.1, 98) * mm});
            skLineSegment(sketch, "E82", {"start": v(-12.99, 98) * mm, "end": v(-12.99, 110) * mm});
            skLineSegment(sketch, "E83", {"start": v(16.1, 98) * mm, "end": v(16.1, 110) * mm});
            skArc(sketch, "E84", {"start": v(16.1, 110) * mm, "mid": v(1.55, 121.31) * mm, "end": v(-12.99, 110) * mm});
            skCircle(sketch, "E85", {"center": v(1.55, 106.31) * mm, "radius": 6 * mm});
            skLineSegment(sketch, "E86", {"start": v(-90, 0) * mm, "end": v(90, 0) * mm, "construction": true});
            skLineSegment(sketch, "E87.MirrorCS", {"start": v(-30.99, -80) * mm, "end": v(-12.99, -98) * mm});
            skLineSegment(sketch, "E88.MirrorCS", {"start": v(-12.99, -98) * mm, "end": v(-12.99, -110) * mm});
            skArc(sketch, "E89.MirrorCS", {"start": v(16.1, -110) * mm, "mid": v(1.55, -121.31) * mm, "end": v(-12.99, -110) * mm});
            skLineSegment(sketch, "E90.MirrorCS", {"start": v(16.1, -98) * mm, "end": v(16.1, -110) * mm});
            skLineSegment(sketch, "E91.MirrorCS", {"start": v(34.1, -80) * mm, "end": v(16.1, -98) * mm});
            skCircle(sketch, "E92.MirrorC", {"center": v(1.55, -106.31) * mm, "radius": 6 * mm});
            skSolve(sketch);
        }
        {
            var Q0;
            {var subQ0=sQuery(id+"F16.wireOp",EDGE,"E87.MirrorCS");Q0=makeQuery(id+"F16.imprint","IMPRINT",FACE,{"disambiguationData":[TD([[makeQuery(id+"F16.imprint","IMPRINT",EDGE,{"derivedFrom":subQ0}),1.0]])]});}
            var Q1;
            {var subQ1=sQuery(id+"F16.wireOp",EDGE,"E80");Q1=makeQuery(id+"F16.imprint","IMPRINT",FACE,{"disambiguationData":[TD([[makeQuery(id+"F16.imprint","IMPRINT",EDGE,{"derivedFrom":subQ1}),-1.0]])]});}
            var Q2;
            {var subQ1=sQuery(id+"F16.wireOp",EDGE,"E79.1");Q2=makeQuery(id+"F16.imprint","IMPRINT",FACE,{"disambiguationData":[TD([[makeQuery(id+"F16.imprint","IMPRINT",EDGE,{"derivedFrom":subQ1}),1.0]])]});}
            extrude(context, id + "F17", {"entities" : qUnion([Q0, Q1, Q2]), "operationType" : NewBodyOperationType.ADD, "depth" : 6.5 * mm});
        }
    });
